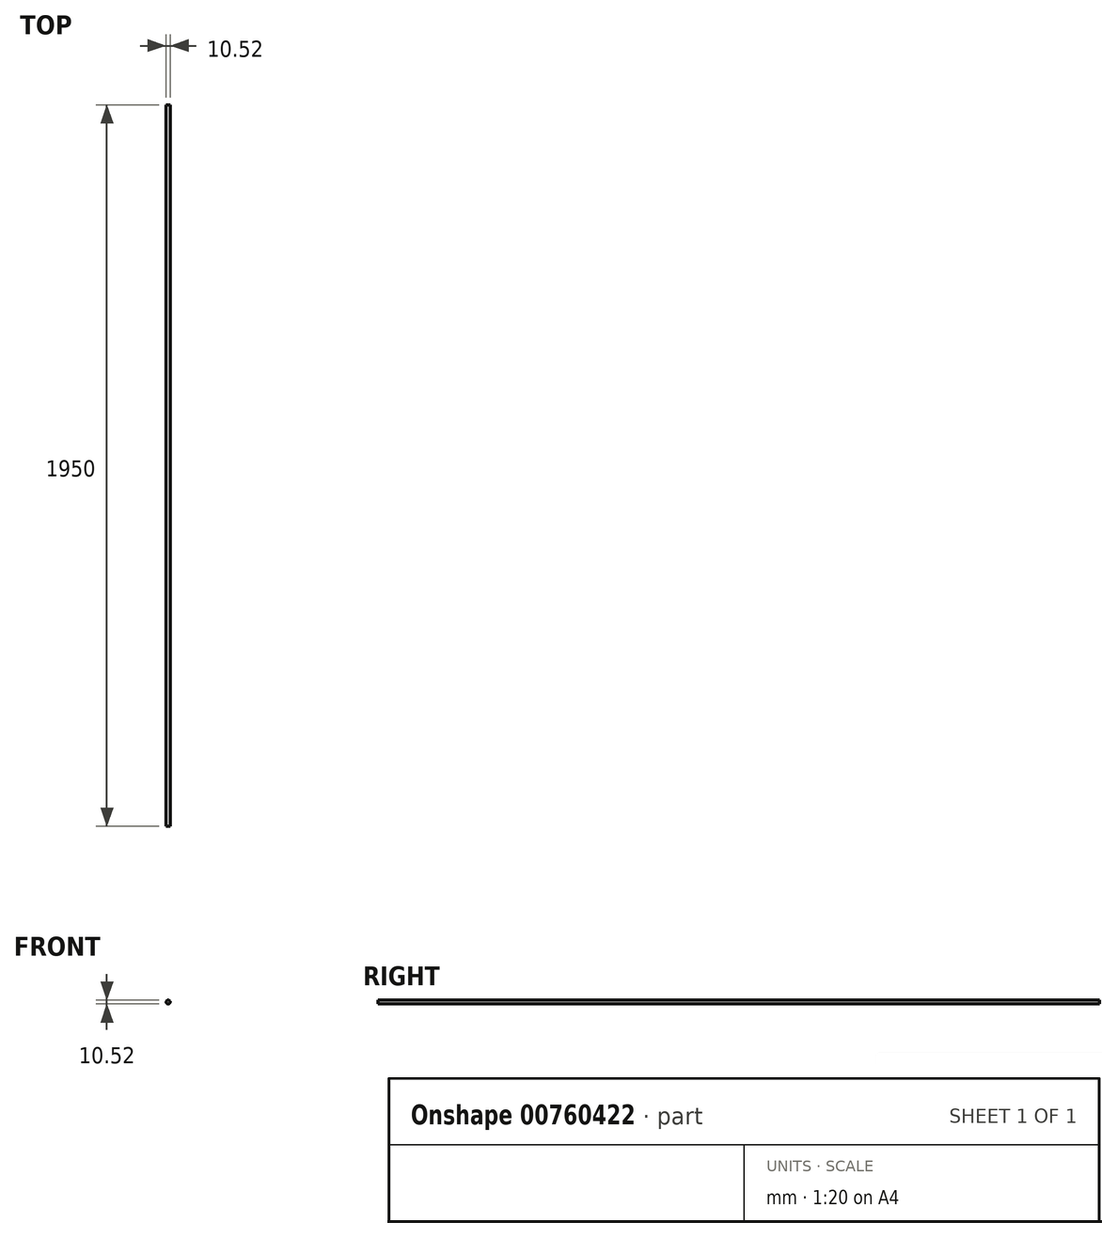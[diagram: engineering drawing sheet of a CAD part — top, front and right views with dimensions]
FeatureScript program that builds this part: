
annotation { "Feature Type Name" : "Feature", "Feature Type Description" : "" }
export const myFeature = defineFeature(function(context is Context, id is Id, definition is map)
    precondition{}
    {
        {
            assignVariable(context, id + "F0", {"name" : "LENGTH", "anyValue" : 1950});
        }
        {
            var Q0;
            Q0=qCreatedBy(makeId("Front.planeOp"),FACE);
            var sketch = newSketch(context, id + "F1", { "sketchPlane" : qUnion([Q0])});
            skCircle(sketch, "E0", {"center": v(0, 0) * mm, "radius": 5.26 * mm});
            skSolve(sketch);
        }
        {
            var Q0;
            Q0=makeQuery(id+"F1.imprint","IMPRINT",FACE,{"disambiguationData":[TD([[makeQuery(id+"F1.imprint","IMPRINT",EDGE,{"derivedFrom":sQuery(id+"F1.wireOp",EDGE,"E0")}),1.0]])]});
            extrude(context, id + "F2", {"entities" : qUnion([Q0]), "oppositeDirection" : true, "depth" : (getVariable(context, 'LENGTH')) * mm, "offsetDistance" : 25 * mm});
        }
    });
